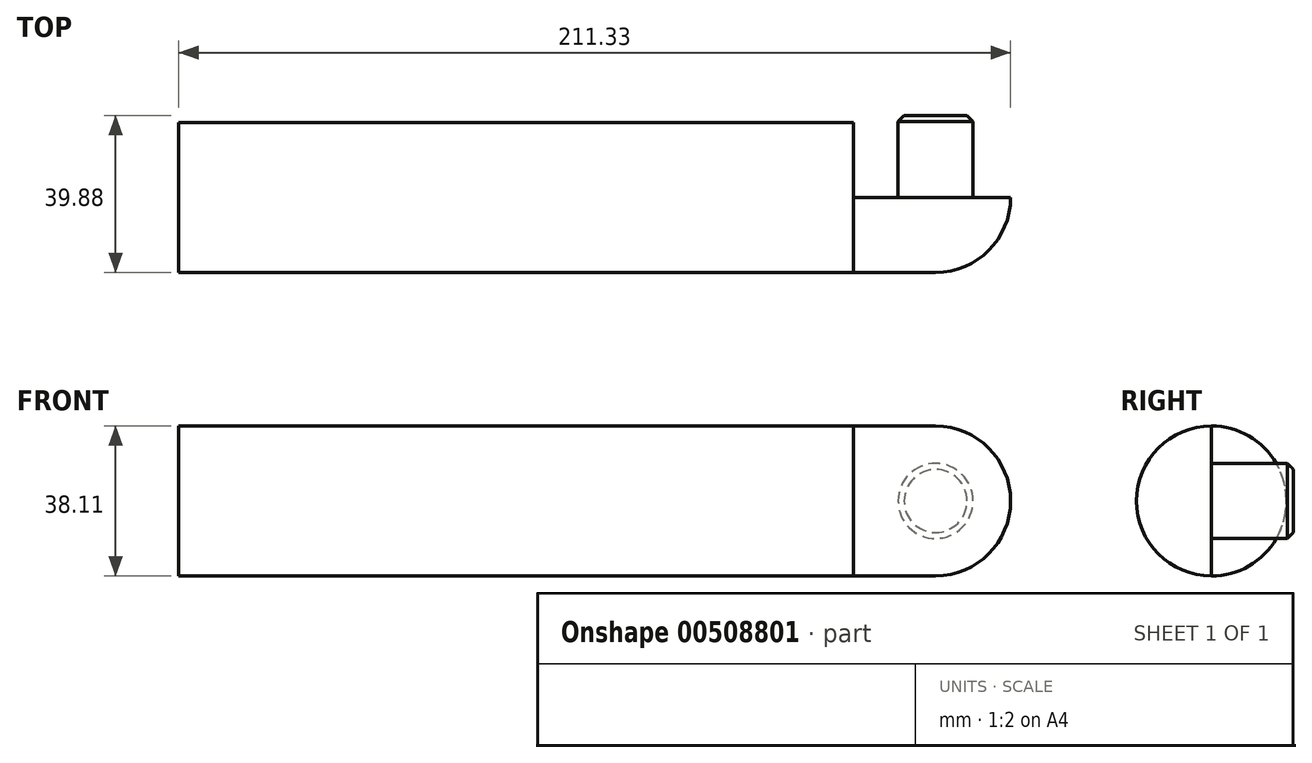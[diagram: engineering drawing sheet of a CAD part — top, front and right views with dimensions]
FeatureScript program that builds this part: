
annotation { "Feature Type Name" : "Feature", "Feature Type Description" : "" }
export const myFeature = defineFeature(function(context is Context, id is Id, definition is map)
    precondition{}
    {
        {
            var Q0;
            Q0=qCreatedBy(makeId("Front.planeOp"),FACE);
            var sketch = newSketch(context, id + "F0", { "sketchPlane" : qUnion([Q0])});
            skLineSegment(sketch, "E0.bottom", {"start": v(-85.72, -9.52) * mm, "end": v(85.72, -9.52) * mm});
            skLineSegment(sketch, "E0.top", {"start": v(-85.73, 9.52) * mm, "end": v(85.72, 9.52) * mm});
            skLineSegment(sketch, "E0.left", {"start": v(-85.73, -9.52) * mm, "end": v(-85.73, 9.52) * mm});
            skLineSegment(sketch, "E0.right", {"start": v(85.72, -9.52) * mm, "end": v(85.72, 9.52) * mm});
            skPoint(sketch, "E0.middle", {"position": v(0, 0) * mm});
            skSolve(sketch);
        }
        {
            var Q0;
            Q0=makeQuery(id+"F0.imprint","IMPRINT",FACE,{"disambiguationData":[TD([[makeQuery(id+"F0.imprint","IMPRINT",EDGE,{"derivedFrom":sQuery(id+"F0.wireOp",EDGE,"E0.bottom")}),1.0]])]});
            var Q1;
            Q1=sQuery(id+"F0.wireOp",EDGE,"E0.bottom");
            revolve(context, id + "F1", {"entities" : qUnion([Q0]), "axis" : qUnion([Q1]), "revolveType" : RevolveType.FULL});
        }
        {
            var Q0;
            Q0=makeQuery(id+"F1.opRevolve","SWEPT_FACE",FACE,{"disambiguationData":[OSD([sQuery(id+"F0.wireOp",EDGE,"E0.right")])]});
            var sketch = newSketch(context, id + "F2", { "sketchPlane" : qUnion([Q0])});
            skLineSegment(sketch, "E1", {"start": v(0, 9.52) * mm, "end": v(0, -28.57) * mm});
            skSolve(sketch);
        }
        {
            var Q0;
            Q0=qSketchRegion(id+"F2",true);
            var Q1;
            {var subQ0=sQuery(id+"F2.wireOp",EDGE,"E1");Q1=makeQuery(id+"F2.imprint","IMPRINT",FACE,{"disambiguationData":[TD([[makeQuery(id+"F2.imprint","IMPRINT",EDGE,{"derivedFrom":subQ0}),-1.0]])]});}
            extrude(context, id + "F3", {"entities" : qUnion([Q0, Q1]), "depth" : 20.83 * mm});
        }
        {
            var Q0;
            Q0=makeQuery(id+"F3.opExtrude","CAP_FACE",FACE,{"disambiguationData":[OSD([sQuery(id+"F0.wireOp",EDGE,"E0.top"),sQuery(id+"F0.wireOp",EDGE,"E0.right"),sQuery(id+"F2.wireOp",EDGE,"E1")])],"isStart":false});
            var sketch = newSketch(context, id + "F4", { "sketchPlane" : qUnion([Q0])});
            skLineSegment(sketch, "E2", {"start": v(0, -9.52) * mm, "end": v(-19.05, -9.52) * mm, "construction": true});
            skSolve(sketch);
        }
        {
            var Q0;
            Q0=qSketchRegion(id+"F4",true);
            var Q1;
            Q1=makeQuery(id+"F4.imprint","IMPRINT",FACE,{"disambiguationData":[TD([[makeQuery(id+"F4.imprint","IMPRINT",EDGE,{"derivedFrom":makeQuery(id+"F3.opExtrude","CAP_EDGE",EDGE,{"disambiguationData":[OSD([sQuery(id+"F2.wireOp",EDGE,"E1")])],"isStart":false})}),-1.0]])]});
            var Q2;
            Q2=makeQuery(id+"F3.opExtrude","CAP_EDGE",EDGE,{"disambiguationData":[OSD([sQuery(id+"F2.wireOp",EDGE,"E1")])],"isStart":false});
            revolve(context, id + "F5", {"operationType" : NewBodyOperationType.ADD, "entities" : qUnion([Q0, Q1]), "axis" : qUnion([Q2]), "revolveType" : RevolveType.ONE_DIRECTION, "oppositeDirection" : true, "angle" : 90 * degree});
        }
        {
            var Q0;
            {var subQ0=sQuery(id+"F2.wireOp",EDGE,"E1");Q0=makeQuery(id+"F5.boolean.opBoolean","MERGE",FACE,{"derivedFrom":[makeQuery(id+"F3.opExtrude","SWEPT_FACE",FACE,{"disambiguationData":[OSD([subQ0])]}),makeQuery(id+"F5.opRevolve","CAP_FACE",FACE,{"disambiguationData":[OSD([sQuery(id+"F0.wireOp",EDGE,"E0.top"),sQuery(id+"F0.wireOp",EDGE,"E0.right"),subQ0])],"isStart":false})]});}
            var sketch = newSketch(context, id + "F6", { "sketchPlane" : qUnion([Q0])});
            skLineSegment(sketch, "E3", {"start": v(-106.55, 9.52) * mm, "end": v(-106.55, -28.57) * mm, "construction": true});
            skCircle(sketch, "E4", {"center": v(-106.55, -9.52) * mm, "radius": 9.53 * mm});
            skSolve(sketch);
        }
        {
            var Q0;
            Q0=makeQuery(id+"F6.imprint","IMPRINT",FACE,{"disambiguationData":[TD([[makeQuery(id+"F6.imprint","IMPRINT",EDGE,{"derivedFrom":sQuery(id+"F6.wireOp",EDGE,"E4")}),1.0]])]});
            extrude(context, id + "F7", {"entities" : qUnion([Q0]), "depth" : 20.83 * mm});
        }
        {
            var Q0;
            Q0=makeQuery(id+"F7.opExtrude","CAP_EDGE",EDGE,{"disambiguationData":[OSD([sQuery(id+"F6.wireOp",EDGE,"E4")])],"isStart":false});
            chamfer(context, id + "F8", {"entities" : qUnion([Q0]), "width" : 1.52 * mm, "tangentPropagation" : true});
        }
    });
